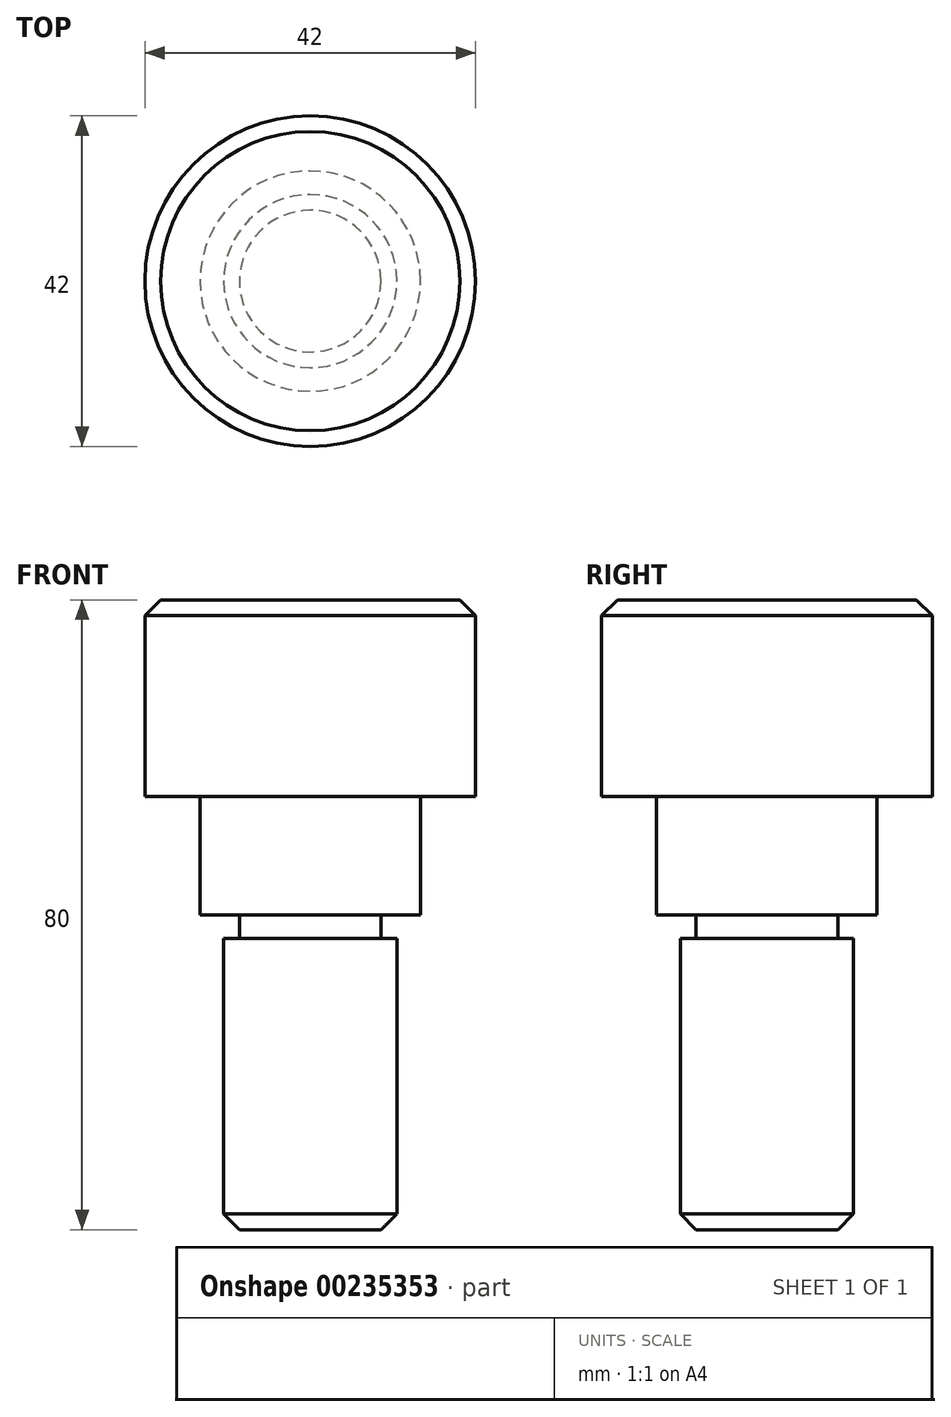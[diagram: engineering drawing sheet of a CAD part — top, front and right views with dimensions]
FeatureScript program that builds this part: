
annotation { "Feature Type Name" : "Feature", "Feature Type Description" : "" }
export const myFeature = defineFeature(function(context is Context, id is Id, definition is map)
    precondition{}
    {
        {
            var Q0;
            Q0=qCreatedBy(makeId("Front.planeOp"),FACE);
            var sketch = newSketch(context, id + "F0", { "sketchPlane" : qUnion([Q0])});
            skLineSegment(sketch, "E0", {"start": v(0, 0) * mm, "end": v(9, 0) * mm});
            skLineSegment(sketch, "E1", {"start": v(9, 0) * mm, "end": v(11, 2) * mm});
            skLineSegment(sketch, "E2", {"start": v(11, 2) * mm, "end": v(11, 37) * mm});
            skLineSegment(sketch, "E3", {"start": v(11, 37) * mm, "end": v(9, 37) * mm});
            skLineSegment(sketch, "E4", {"start": v(9, 37) * mm, "end": v(9, 40) * mm});
            skLineSegment(sketch, "E5", {"start": v(9, 40) * mm, "end": v(14, 40) * mm});
            skLineSegment(sketch, "E6", {"start": v(14, 40) * mm, "end": v(14, 55) * mm});
            skLineSegment(sketch, "E7", {"start": v(14, 55) * mm, "end": v(21, 55) * mm});
            skLineSegment(sketch, "E8", {"start": v(21, 55) * mm, "end": v(21, 78) * mm});
            skLineSegment(sketch, "E9", {"start": v(21, 78) * mm, "end": v(19, 80) * mm});
            skLineSegment(sketch, "E10", {"start": v(19, 80) * mm, "end": v(0, 80) * mm});
            skLineSegment(sketch, "E11", {"start": v(0, -1.2) * mm, "end": v(0, 80) * mm, "construction": true});
            skLineSegment(sketch, "E12", {"start": v(0, 80) * mm, "end": v(0, 0) * mm});
            skSolve(sketch);
        }
        {
            var Q0;
            Q0=makeQuery(id+"F0.imprint","IMPRINT",FACE,{"disambiguationData":[TD([[makeQuery(id+"F0.imprint","IMPRINT",EDGE,{"derivedFrom":sQuery(id+"F0.wireOp",EDGE,"E0")}),1.0]])]});
            var Q1;
            Q1=sQuery(id+"F0.wireOp",EDGE,"E12");
            revolve(context, id + "F1", {"entities" : qUnion([Q0]), "axis" : qUnion([Q1]), "revolveType" : RevolveType.FULL});
        }
    });
